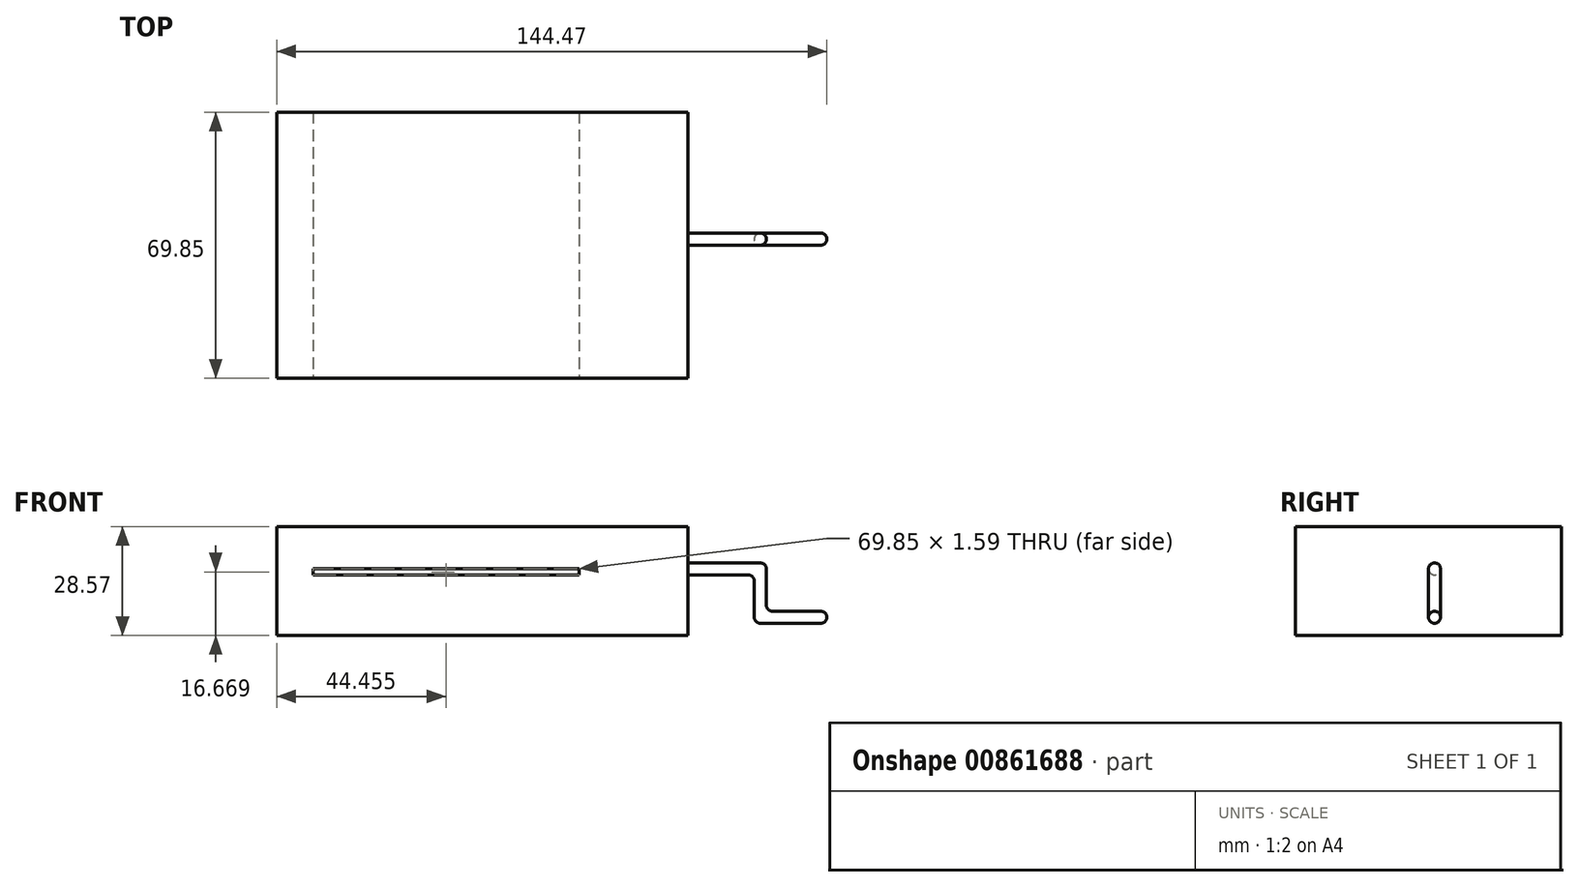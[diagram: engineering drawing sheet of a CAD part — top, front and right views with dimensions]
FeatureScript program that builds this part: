
annotation { "Feature Type Name" : "Feature", "Feature Type Description" : "" }
export const myFeature = defineFeature(function(context is Context, id is Id, definition is map)
    precondition{}
    {
        {
            var Q0;
            Q0=qCreatedBy(makeId("Top.planeOp"),FACE);
            var sketch = newSketch(context, id + "F0", { "sketchPlane" : qUnion([Q0])});
            skLineSegment(sketch, "E0", {"start": v(0, 0) * mm, "end": v(53.98, 0) * mm});
            skLineSegment(sketch, "E1", {"start": v(53.98, 0) * mm, "end": v(53.98, 34.93) * mm});
            skLineSegment(sketch, "E2", {"start": v(53.98, 34.93) * mm, "end": v(-53.98, 34.93) * mm});
            skLineSegment(sketch, "E3", {"start": v(-53.98, 34.93) * mm, "end": v(-53.98, -34.93) * mm});
            skLineSegment(sketch, "E4", {"start": v(-53.98, -34.93) * mm, "end": v(53.97, -34.93) * mm});
            skLineSegment(sketch, "E5", {"start": v(53.97, -34.93) * mm, "end": v(53.97, 0) * mm});
            skSolve(sketch);
        }
        {
            var Q0;
            Q0=makeQuery(id+"F0.imprint","IMPRINT",FACE,{"disambiguationData":[TD([[makeQuery(id+"F0.imprint","IMPRINT",EDGE,{"derivedFrom":sQuery(id+"F0.wireOp",EDGE,"E1")}),1.0]])]});
            extrude(context, id + "F1", {"entities" : qUnion([Q0]), "depth" : 28.57 * mm, "offsetDistance" : 25.4 * mm});
        }
        {
            var Q0;
            Q0=makeQuery(id+"F1.opExtrude","SWEPT_FACE",FACE,{"disambiguationData":[OSD([sQuery(id+"F0.wireOp",EDGE,"E4")])]});
            var sketch = newSketch(context, id + "F2", { "sketchPlane" : qUnion([Q0])});
            skLineSegment(sketch, "E6", {"start": v(-53.98, 0) * mm, "end": v(-53.98, 15.88) * mm});
            skLineSegment(sketch, "E7", {"start": v(-53.98, 15.88) * mm, "end": v(-44.45, 15.88) * mm});
            skLineSegment(sketch, "E8", {"start": v(-44.45, 15.88) * mm, "end": v(25.4, 15.88) * mm});
            skLineSegment(sketch, "E9", {"start": v(25.4, 15.88) * mm, "end": v(25.4, 17.46) * mm});
            skLineSegment(sketch, "E10", {"start": v(25.4, 17.46) * mm, "end": v(-44.45, 17.46) * mm});
            skLineSegment(sketch, "E11", {"start": v(-44.45, 17.46) * mm, "end": v(-44.45, 15.88) * mm});
            skSolve(sketch);
        }
        {
            var Q0;
            Q0=makeQuery(id+"F2.imprint","IMPRINT",FACE,{"disambiguationData":[TD([[makeQuery(id+"F2.imprint","IMPRINT",EDGE,{"derivedFrom":sQuery(id+"F2.wireOp",EDGE,"E8")}),1.0]])]});
            var Q1;
            Q1=makeQuery(id+"F1.opExtrude","SWEPT_FACE",FACE,{"disambiguationData":[OSD([sQuery(id+"F0.wireOp",EDGE,"E2")])]});
            extrude(context, id + "F3", {"entities" : qUnion([Q0]), "operationType" : NewBodyOperationType.REMOVE, "endBound" : BoundingType.UP_TO_SURFACE, "oppositeDirection" : true, "depth" : 25.4 * mm, "endBoundEntityFace" : qUnion([Q1]), "offsetDistance" : 25.4 * mm});
        }
        {
            var Q0;
            Q0=makeQuery(id+"F1.opExtrude","SWEPT_FACE",FACE,{"disambiguationData":[OSD([sQuery(id+"F0.wireOp",EDGE,"E4")])]});
            cPlane(context, id + "F4", {"entities" : qUnion([Q0]), "cplaneType" : CPlaneType.OFFSET, "offset" : 36.5 * mm, "oppositeDirection" : true, "width" : 152.4 * mm, "height" : 152.4 * mm});
        }
        {
            var Q0;
            Q0=qCreatedBy(id+"F4.planeOp",FACE);
            var sketch = newSketch(context, id + "F5", { "sketchPlane" : qUnion([Q0])});
            skLineSegment(sketch, "E12", {"start": v(0, 0) * mm, "end": v(53.97, 0) * mm});
            skLineSegment(sketch, "E13", {"start": v(53.98, 0) * mm, "end": v(53.98, 15.88) * mm});
            skLineSegment(sketch, "E14", {"start": v(53.98, 15.88) * mm, "end": v(71.44, 15.88) * mm});
            skLineSegment(sketch, "E15", {"start": v(71.44, 15.88) * mm, "end": v(71.44, 3.17) * mm});
            skLineSegment(sketch, "E16", {"start": v(71.44, 3.17) * mm, "end": v(90.49, 3.17) * mm});
            skLineSegment(sketch, "E17", {"start": v(90.49, 3.17) * mm, "end": v(90.49, 6.35) * mm});
            skLineSegment(sketch, "E18", {"start": v(90.49, 6.35) * mm, "end": v(74.61, 6.35) * mm});
            skLineSegment(sketch, "E19", {"start": v(74.61, 6.35) * mm, "end": v(74.61, 19.05) * mm});
            skLineSegment(sketch, "E20", {"start": v(74.61, 19.05) * mm, "end": v(53.97, 19.05) * mm});
            skLineSegment(sketch, "E21", {"start": v(53.97, 15.88) * mm, "end": v(53.97, 19.05) * mm});
            skSolve(sketch);
        }
        {
            var Q0;
            Q0=makeQuery(id+"F5.imprint","IMPRINT",FACE,{"disambiguationData":[TD([[makeQuery(id+"F5.imprint","IMPRINT",EDGE,{"derivedFrom":sQuery(id+"F5.wireOp",EDGE,"E14")}),1.0]])]});
            extrude(context, id + "F6", {"entities" : qUnion([Q0]), "operationType" : NewBodyOperationType.ADD, "depth" : 1.59 * mm, "offsetDistance" : 25.4 * mm, "hasSecondDirection" : true, "secondDirectionOppositeDirection" : true, "secondDirectionDepth" : 1.59 * mm});
        }
        {
            var Q0;
            Q0=makeQuery(id+"F6.opExtrude","CAP_EDGE",EDGE,{"disambiguationData":[OSD([sQuery(id+"F5.wireOp",EDGE,"E20")])],"isStart":false});
            var Q1;
            Q1=makeQuery(id+"F6.opExtrude","CAP_EDGE",EDGE,{"disambiguationData":[OSD([sQuery(id+"F5.wireOp",EDGE,"E19")])],"isStart":true});
            var Q2;
            Q2=makeQuery(id+"F6.opExtrude","CAP_EDGE",EDGE,{"disambiguationData":[OSD([sQuery(id+"F5.wireOp",EDGE,"E19")])],"isStart":false});
            var Q3;
            Q3=makeQuery(id+"F6.opExtrude","SWEPT_EDGE",EDGE,{"disambiguationData":[OSD([sQuery(id+"F5.wireOp",EDGE,"E19"),sQuery(id+"F5.wireOp",EDGE,"E20")])]});
            var Q4;
            Q4=makeQuery(id+"F6.opExtrude","SWEPT_EDGE",EDGE,{"disambiguationData":[OSD([sQuery(id+"F5.wireOp",EDGE,"E18"),sQuery(id+"F5.wireOp",EDGE,"E19")])]});
            var Q5;
            Q5=makeQuery(id+"F6.opExtrude","CAP_EDGE",EDGE,{"disambiguationData":[OSD([sQuery(id+"F5.wireOp",EDGE,"E15")])],"isStart":false});
            var Q6;
            Q6=makeQuery(id+"F6.opExtrude","CAP_EDGE",EDGE,{"disambiguationData":[OSD([sQuery(id+"F5.wireOp",EDGE,"E14")])],"isStart":false});
            var Q7;
            Q7=makeQuery(id+"F6.opExtrude","CAP_EDGE",EDGE,{"disambiguationData":[OSD([sQuery(id+"F5.wireOp",EDGE,"E20")])],"isStart":true});
            var Q8;
            Q8=makeQuery(id+"F6.opExtrude","CAP_EDGE",EDGE,{"disambiguationData":[OSD([sQuery(id+"F5.wireOp",EDGE,"E18")])],"isStart":true});
            var Q9;
            Q9=makeQuery(id+"F6.opExtrude","CAP_EDGE",EDGE,{"disambiguationData":[OSD([sQuery(id+"F5.wireOp",EDGE,"E18")])],"isStart":false});
            var Q10;
            Q10=makeQuery(id+"F6.opExtrude","CAP_EDGE",EDGE,{"disambiguationData":[OSD([sQuery(id+"F5.wireOp",EDGE,"E16")])],"isStart":false});
            var Q11;
            Q11=makeQuery(id+"F6.opExtrude","SWEPT_EDGE",EDGE,{"disambiguationData":[OSD([sQuery(id+"F5.wireOp",EDGE,"E16"),sQuery(id+"F5.wireOp",EDGE,"E17")])]});
            var Q12;
            Q12=makeQuery(id+"F6.opExtrude","CAP_EDGE",EDGE,{"disambiguationData":[OSD([sQuery(id+"F5.wireOp",EDGE,"E17")])],"isStart":false});
            var Q13;
            Q13=makeQuery(id+"F6.opExtrude","SWEPT_EDGE",EDGE,{"disambiguationData":[OSD([sQuery(id+"F5.wireOp",EDGE,"E17"),sQuery(id+"F5.wireOp",EDGE,"E18")])]});
            var Q14;
            Q14=makeQuery(id+"F6.opExtrude","CAP_EDGE",EDGE,{"disambiguationData":[OSD([sQuery(id+"F5.wireOp",EDGE,"E17")])],"isStart":true});
            var Q15;
            Q15=makeQuery(id+"F6.opExtrude","CAP_EDGE",EDGE,{"disambiguationData":[OSD([sQuery(id+"F5.wireOp",EDGE,"E14")])],"isStart":true});
            var Q16;
            Q16=makeQuery(id+"F6.opExtrude","SWEPT_EDGE",EDGE,{"disambiguationData":[OSD([sQuery(id+"F5.wireOp",EDGE,"E15"),sQuery(id+"F5.wireOp",EDGE,"E16")])]});
            var Q17;
            Q17=makeQuery(id+"F6.opExtrude","CAP_EDGE",EDGE,{"disambiguationData":[OSD([sQuery(id+"F5.wireOp",EDGE,"E16")])],"isStart":true});
            var Q18;
            Q18=makeQuery(id+"F6.opExtrude","CAP_EDGE",EDGE,{"disambiguationData":[OSD([sQuery(id+"F5.wireOp",EDGE,"E15")])],"isStart":true});
            var Q19;
            Q19=makeQuery(id+"F6.opExtrude","SWEPT_EDGE",EDGE,{"disambiguationData":[OSD([sQuery(id+"F5.wireOp",EDGE,"E14"),sQuery(id+"F5.wireOp",EDGE,"E15")])]});
            fillet(context, id + "F7", {"entities" : qUnion([Q0, Q1, Q2, Q3, Q4, Q5, Q6, Q7, Q8, Q9, Q10, Q11, Q12, Q13, Q14, Q15, Q16, Q17, Q18, Q19]), "radius" : 1.59 * mm, "tangentPropagation" : true, "allowEdgeOverflow" : false});
        }
    });
